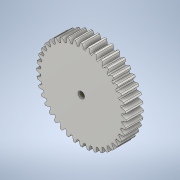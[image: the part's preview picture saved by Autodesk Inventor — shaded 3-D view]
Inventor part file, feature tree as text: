
AUTODESK INVENTOR PART (.ipt)
format: ipt  version: 2021 (Build 250183000, 183)  size: 313,344 bytes
history: native  units: mm (DEFAULTED — no unit token found)
features: sketch x4, plane x3, other x3, extrude x1, hole x1
ambient origin geometry x8: Origin, YZ Plane, XZ Plane, XY Plane, X Axis, Y Axis, Z Axis, Center Point
bodies: Solid1 (feature_tree)
feature tree (12):
  extrude  "Extrusion1"  Depth=8.0mm TaperAngle=0.0deg
  plane  "Work Plane2"
  plane  "Work Plane8"
  plane  "Work Plane9"
  other  "Spur Gear"
  sketch  "Sketch3"  dims[d16=25.351695mm]
  hole  "Hole1"  [1 undecoded]
  sketch  "Sketch1"  dims[d0=41.564361mm d1=8.0mm d2=0.0mm]
  sketch  "Sketch2"  dims[d3=40.0mm d4=10.0mm d5=0.0mm]
  other  "Srf1"
  sketch  "Sketch4"  dims[d17=0.0mm d34=0.785398mm d39=0.0mm d41=0.0mm d43=25.351695mm d46=25.351695mm d47=0.0mm d48=0.0mm d49=3.0mm d50=3.0mm d51=6.0mm d52=4.0mm d53=2.0mm d54=90.0deg d55=8.0mm d56=20.594885mm]
  other  "Pitch Diameter"
note: 1 required parameter value undecoded (feature->parameter linkage not recoverable at this tier; creation-order binding heuristic only, values carry confidence <= 0.55)
